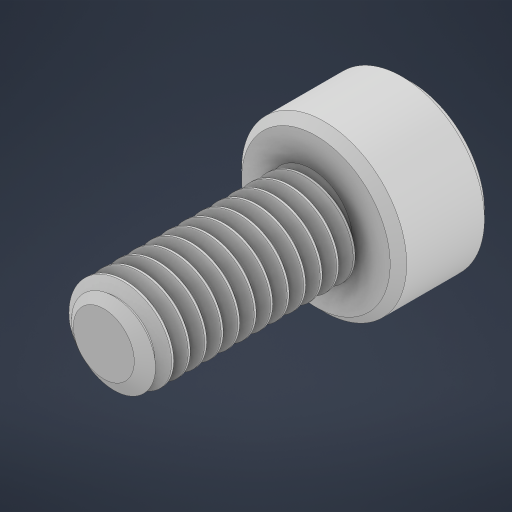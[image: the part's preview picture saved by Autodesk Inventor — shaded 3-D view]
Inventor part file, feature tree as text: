
AUTODESK INVENTOR PART (.ipt)
format: ipt  version: 2023 (Build 270158000, 158)  size: 603,136 bytes
history: native  units: in
note: dims shown in document units (in); Inventor stores cm internally (conversion verified against a paired STEP export)
features: chamfer x1
ambient origin geometry x8: Origin, YZ Plane, XZ Plane, XY Plane, X Axis, Y Axis, Z Axis, Center Point
bodies: Solid1 (feature_tree)
feature tree (1):
  chamfer  "Chamfer1"  [1 undecoded]
note: 1 required parameter value undecoded (feature->parameter linkage not recoverable at this tier; creation-order binding heuristic only, values carry confidence <= 0.55)
